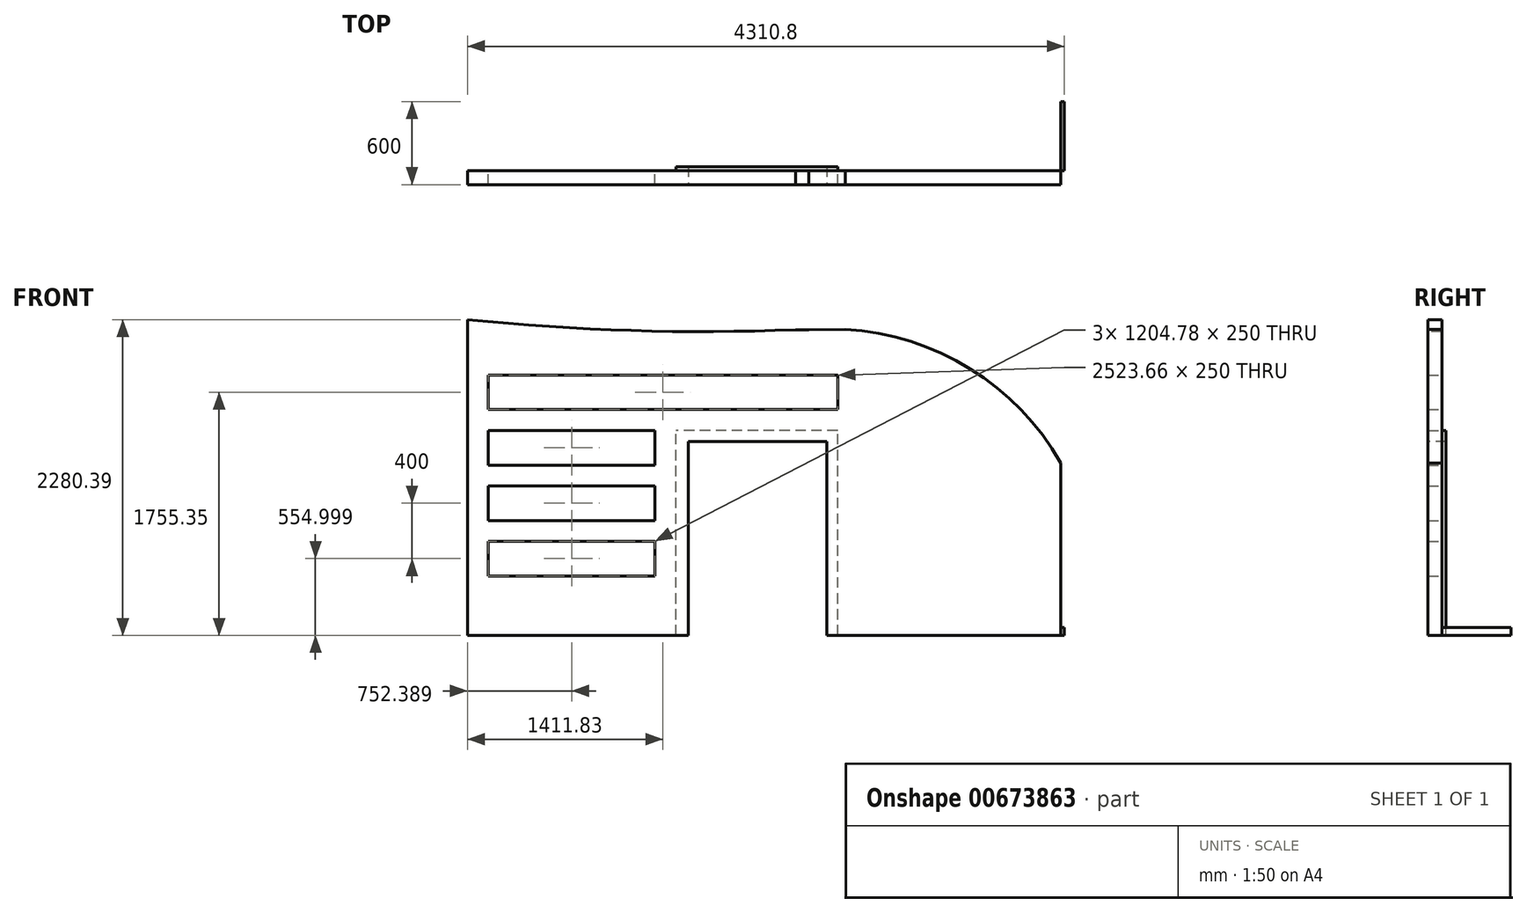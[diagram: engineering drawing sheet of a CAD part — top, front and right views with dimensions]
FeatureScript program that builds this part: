
annotation { "Feature Type Name" : "Feature", "Feature Type Description" : "" }
export const myFeature = defineFeature(function(context is Context, id is Id, definition is map)
    precondition{}
    {
        {
            var Q0;
            Q0=qCreatedBy(makeId("Front.planeOp"),FACE);
            var sketch = newSketch(context, id + "F0", { "sketchPlane" : qUnion([Q0])});
            skArc(sketch, "E0", {"start": v(1976.28, -75) * mm, "mid": v(1320.1, 604.94) * mm, "end": v(419.38, 890.65) * mm});
            skArc(sketch, "E1", {"start": v(-2409.52, 970.96) * mm, "mid": v(-1175.98, 883.32) * mm, "end": v(60.66, 887.71) * mm});
            skLineSegment(sketch, "E2", {"start": v(1976.28, -75) * mm, "end": v(1976.28, -1320) * mm});
            skLineSegment(sketch, "E3", {"start": v(154.47, 887.71) * mm, "end": v(419.38, 890.65) * mm});
            skLineSegment(sketch, "E4", {"start": v(1976.28, -1320) * mm, "end": v(-2409.52, -1320) * mm});
            skLineSegment(sketch, "E5", {"start": v(-2409.52, -1320) * mm, "end": v(-2409.52, 970.96) * mm});
            skLineSegment(sketch, "E6", {"start": v(-215.86, 80) * mm, "end": v(-715.86, 80) * mm});
            skLineSegment(sketch, "E7", {"start": v(-215.86, 80) * mm, "end": v(284.14, 80) * mm});
            skLineSegment(sketch, "E8", {"start": v(284.14, 80) * mm, "end": v(284.14, -1320) * mm});
            skLineSegment(sketch, "E9", {"start": v(-715.86, 80) * mm, "end": v(-715.86, -1320) * mm});
            skLineSegment(sketch, "E10", {"start": v(-715.86, -1320) * mm, "end": v(-804.74, -1320) * mm});
            skLineSegment(sketch, "E11", {"start": v(284.14, 160) * mm, "end": v(-715.86, 160) * mm});
            skLineSegment(sketch, "E12", {"start": v(-804.74, -1320) * mm, "end": v(-804.74, 160) * mm});
            skLineSegment(sketch, "E13", {"start": v(-715.86, 160) * mm, "end": v(-804.74, 160) * mm});
            skPoint(sketch, "E14.end.orphan", {"position": v(284.14, 160) * mm});
            skLineSegment(sketch, "E15", {"start": v(60.66, 887.71) * mm, "end": v(154.47, 887.71) * mm});
            skPoint(sketch, "E16.orphan", {"position": v(398.49, 160) * mm});
            skLineSegment(sketch, "E17", {"start": v(284.14, -1320) * mm, "end": v(364.14, -1320) * mm});
            skLineSegment(sketch, "E18", {"start": v(364.14, -1320) * mm, "end": v(364.14, 160) * mm});
            skLineSegment(sketch, "E19", {"start": v(284.14, 160) * mm, "end": v(364.14, 160) * mm});
            skLineSegment(sketch, "E20", {"start": v(-215.86, 80) * mm, "end": v(-225.86, 80) * mm});
            skLineSegment(sketch, "E21", {"start": v(-215.86, 80) * mm, "end": v(-205.86, 80) * mm});
            skLineSegment(sketch, "E22", {"start": v(-205.86, 80) * mm, "end": v(-205.86, -1320) * mm});
            skLineSegment(sketch, "E23", {"start": v(-225.86, 80) * mm, "end": v(-225.86, -1320) * mm});
            skSolve(sketch);
        }
        {
            var Q0;
            Q0=makeQuery(id+"F0.imprint","IMPRINT",FACE,{"disambiguationData":[TD([[makeQuery(id+"F0.imprint","IMPRINT",EDGE,{"derivedFrom":sQuery(id+"F0.wireOp",EDGE,"E0")}),1.0]])]});
            extrude(context, id + "F1", {"entities" : qUnion([Q0]), "oppositeDirection" : true, "depth" : 100 * mm, "offsetDistance" : 25 * mm});
        }
        {
            var Q0;
            Q0=makeQuery(id+"F0.imprint","IMPRINT",FACE,{"disambiguationData":[TD([[makeQuery(id+"F0.imprint","IMPRINT",EDGE,{"derivedFrom":sQuery(id+"F0.wireOp",EDGE,"E6")}),-1.0]])]});
            extrude(context, id + "F2", {"entities" : qUnion([Q0]), "operationType" : NewBodyOperationType.ADD, "oppositeDirection" : true, "depth" : 130 * mm, "offsetDistance" : 25 * mm});
        }
        {
            var Q0;
            Q0=makeQuery(id+"F1.opExtrude","SWEPT_FACE",FACE,{"disambiguationData":[OSD([sQuery(id+"F0.wireOp",EDGE,"E2")])]});
            var sketch = newSketch(context, id + "F3", { "sketchPlane" : qUnion([Q0])});
            skLineSegment(sketch, "E24.bottom", {"start": v(100, -1320) * mm, "end": v(600, -1320) * mm});
            skLineSegment(sketch, "E24.top", {"start": v(100, -1261.6) * mm, "end": v(600, -1261.6) * mm});
            skLineSegment(sketch, "E24.left", {"start": v(100, -1320) * mm, "end": v(100, -1261.6) * mm});
            skLineSegment(sketch, "E24.right", {"start": v(600, -1320) * mm, "end": v(600, -1261.6) * mm});
            skSolve(sketch);
        }
        {
            var Q0;
            Q0=makeQuery(id+"F3.imprint","IMPRINT",FACE,{"disambiguationData":[TD([[makeQuery(id+"F3.imprint","IMPRINT",EDGE,{"derivedFrom":sQuery(id+"F3.wireOp",EDGE,"E24.bottom")}),1.0]])]});
            extrude(context, id + "F4", {"entities" : qUnion([Q0]), "depth" : 25 * mm, "offsetDistance" : 25 * mm});
        }
        {
            var Q0;
            Q0=makeQuery(id+"F1.opExtrude","SWEPT_FACE",FACE,{"disambiguationData":[OSD([sQuery(id+"F0.wireOp",EDGE,"E5")])]});
            extrude(context, id + "F5", {"entities" : qUnion([Q0]), "operationType" : NewBodyOperationType.REMOVE, "oppositeDirection" : true, "depth" : 100 * mm, "offsetDistance" : 25 * mm});
        }
        {
            var Q0;
            Q0=makeQuery(id+"F1.opExtrude","CAP_FACE",FACE,{"disambiguationData":[OSD([sQuery(id+"F0.wireOp",EDGE,"E0"),sQuery(id+"F0.wireOp",EDGE,"E1"),sQuery(id+"F0.wireOp",EDGE,"E2"),sQuery(id+"F0.wireOp",EDGE,"E3"),sQuery(id+"F0.wireOp",EDGE,"E4"),sQuery(id+"F0.wireOp",EDGE,"E5"),sQuery(id+"F0.wireOp",EDGE,"E11"),sQuery(id+"F0.wireOp",EDGE,"E12"),sQuery(id+"F0.wireOp",EDGE,"E13"),sQuery(id+"F0.wireOp",EDGE,"E15"),sQuery(id+"F0.wireOp",EDGE,"E18"),sQuery(id+"F0.wireOp",EDGE,"E19")])],"isStart":false});
            var sketch = newSketch(context, id + "F6", { "sketchPlane" : qUnion([Q0])});
            skLineSegment(sketch, "E25", {"start": v(2159.52, -90) * mm, "end": v(2159.52, 160) * mm});
            skLineSegment(sketch, "E26", {"start": v(2159.52, -226.07) * mm, "end": v(2159.52, -490) * mm});
            skLineSegment(sketch, "E27.bottom", {"start": v(-364.14, 560.36) * mm, "end": v(2159.52, 560.36) * mm});
            skLineSegment(sketch, "E27.top", {"start": v(-364.14, 310.36) * mm, "end": v(2159.52, 310.36) * mm});
            skLineSegment(sketch, "E27.left", {"start": v(-364.14, 560.36) * mm, "end": v(-364.14, 310.36) * mm});
            skLineSegment(sketch, "E27.right", {"start": v(2159.52, 560.36) * mm, "end": v(2159.52, 310.36) * mm});
            skLineSegment(sketch, "E28.bottom", {"start": v(954.74, 160) * mm, "end": v(2159.52, 160) * mm});
            skLineSegment(sketch, "E28.top", {"start": v(954.74, -90) * mm, "end": v(2159.52, -90) * mm});
            skLineSegment(sketch, "E28.left", {"start": v(954.74, 160) * mm, "end": v(954.74, -90) * mm});
            skLineSegment(sketch, "E28.right", {"start": v(2159.52, 160) * mm, "end": v(2159.52, -90) * mm});
            skLineSegment(sketch, "E29.bottom", {"start": v(954.74, -240) * mm, "end": v(2159.52, -240) * mm});
            skLineSegment(sketch, "E29.top", {"start": v(954.74, -490) * mm, "end": v(2159.52, -490) * mm});
            skLineSegment(sketch, "E29.left", {"start": v(954.74, -240) * mm, "end": v(954.74, -490) * mm});
            skLineSegment(sketch, "E29.right", {"start": v(2159.52, -240) * mm, "end": v(2159.52, -490) * mm});
            skLineSegment(sketch, "E30.bottom", {"start": v(954.74, -640) * mm, "end": v(2159.52, -640) * mm});
            skLineSegment(sketch, "E30.top", {"start": v(954.74, -890) * mm, "end": v(2159.52, -890) * mm});
            skLineSegment(sketch, "E30.left", {"start": v(954.74, -640) * mm, "end": v(954.74, -890) * mm});
            skLineSegment(sketch, "E30.right", {"start": v(2159.52, -640) * mm, "end": v(2159.52, -890) * mm});
            skPoint(sketch, "E31.orphan", {"position": v(2159.52, 846.79) * mm});
            skLineSegment(sketch, "E32.trimOffspring", {"start": v(2159.52, 310.36) * mm, "end": v(2159.52, 560.36) * mm});
            skPoint(sketch, "E33.orphan", {"position": v(2159.52, -1320) * mm});
            skSolve(sketch);
        }
        {
            var Q0;
            Q0=makeQuery(id+"F6.imprint","IMPRINT",FACE,{"disambiguationData":[TD([[makeQuery(id+"F6.imprint","IMPRINT",EDGE,{"derivedFrom":sQuery(id+"F6.wireOp",EDGE,"E27.bottom")}),-1.0]])]});
            var Q1;
            Q1=makeQuery(id+"F6.imprint","IMPRINT",FACE,{"disambiguationData":[TD([[makeQuery(id+"F6.imprint","IMPRINT",EDGE,{"derivedFrom":sQuery(id+"F6.wireOp",EDGE,"E28.bottom")}),-1.0]])]});
            var Q2;
            Q2=makeQuery(id+"F6.imprint","IMPRINT",FACE,{"disambiguationData":[TD([[makeQuery(id+"F6.imprint","IMPRINT",EDGE,{"derivedFrom":sQuery(id+"F6.wireOp",EDGE,"E29.bottom")}),-1.0]])]});
            var Q3;
            Q3=makeQuery(id+"F6.imprint","IMPRINT",FACE,{"disambiguationData":[TD([[makeQuery(id+"F6.imprint","IMPRINT",EDGE,{"derivedFrom":sQuery(id+"F6.wireOp",EDGE,"E30.bottom")}),-1.0]])]});
            extrude(context, id + "F7", {"entities" : qUnion([Q0, Q1, Q2, Q3]), "operationType" : NewBodyOperationType.REMOVE, "oppositeDirection" : true, "depth" : 2010 * mm, "offsetDistance" : 25 * mm});
        }
    });
